# Revit family: Gleiter GL-37
name_source: partatom
category: HLS-Bauteile
revit_build: Autodesk Revit 2017 (Build: 20190507_1515(x64)
units: mm (PartAtom-declared; Revit-internal decimal feet)

## family parameters
Arbeitsebenenbasiert = Ja
Beim Laden mit Abzugskörper schneiden = Nein
Bemaßung runder Anschluss = Durchmesser verwenden
Gemeinsam genutzt = Ja
Immer vertikal = Nein
Raumberechnungspunkt = Nein
Teiletyp = Normal

## types (5) — shared parameters
Anzahl Anschlüsse = 1
Breite = 65 mm  [stored 0.213255 ft]
Fabrikat = MEFA
Firma = MEFA Befestigungs- und Montagesysteme GmbH
Gleitreibungsfaktor = 0.15 - 0.25
Haftreibungsfaktor = 0,2 - 0,3
Kurztext1 = Gleiter axial GL 37
Lochdurchmesser = 12.5 mm
Länge = 72 mm  [stored 0.23622 ft]
Material Gleitelement = Stahl
Material Gleitstreifen = Kunststoff
Materialname Gleitelement = S235JR
Materialname Gleitstreifen = Polyamid 6
Mengeneinheit = St
Vorgabe-Ansicht = 1219 mm
max. Schiebeweg axial = 37 mm
max. Temperaturbeständigkeit = 100 °C
max. zul. Last hängend = 1.30 kN
max. zul. Last stehend = 1.30 kN
vpe = 25 St

## per-type parameters (varying)
| type | Anschluss | Artikelnummer | Bauhöhe | EAN | Gewicht | Gewicht pro Bauteil | Gewinde | Gewindeanschlüsse | H | Kurztext2 |
| Gleiter GL- 37, M 8 | 1 x M8 | 0770515 | 32 mm | 4250928417848 | 0.20 kg | 0.20 kg | M8 | 6kt-Mutter parametrik : Hutmutter gedreht M8 (4130008) | 32 mm  [stored 0.104987 ft] | Anschluss 1 x M8 |
| Gleiter GL- 37, M10 | 1 x M10 | 0770523 | 34 mm | 4250928417855 | 0.21 kg | 0.21 kg | M10 | 6kt-Mutter parametrik : Hutmutter gedreht M10 (4130010) | 34 mm | Anschluss 1 x M10 |
| Gleiter GL- 37, M12 | 1 x M12 | 0770531 | 36 mm | 4250928417916 | 0.22 kg | 0.22 kg | M12 | 6kt-Mutter parametrik : Hutmutter gedreht M12 (4130012) | 36 mm  [stored 0.11811 ft] | Anschluss 1 x M12 |
| Gleiter GL- 37, M16 | 1 x M16 | 0770558 | 34 mm | 4250928418029 | 0.23 kg | 0.23 kg | M16 | 6kt-Mutter parametrik : Hutmutter M16 (4130016) | 34 mm | Anschluss 1 x M16 |
| Gleiter GL-37, 1/2" | 1 x 1/2'' | 0770604 | 35 mm | 4250928418098 | 0.23 kg | 0.23 kg | 1/2'' | Runde Gewindeanschlusse parametrik : Muffe 1/2´´ (0009865) | 35 mm  [stored 0.114829 ft] | Anschluss 1 x 1/2'' |

note: [stored X ft] marks values corroborated as IEEE doubles in the binary element streams (Revit-internal decimal feet)

## geometry (parser evidence)
native form markers: Sweep x3
no freeform markers — native parametric forms only
